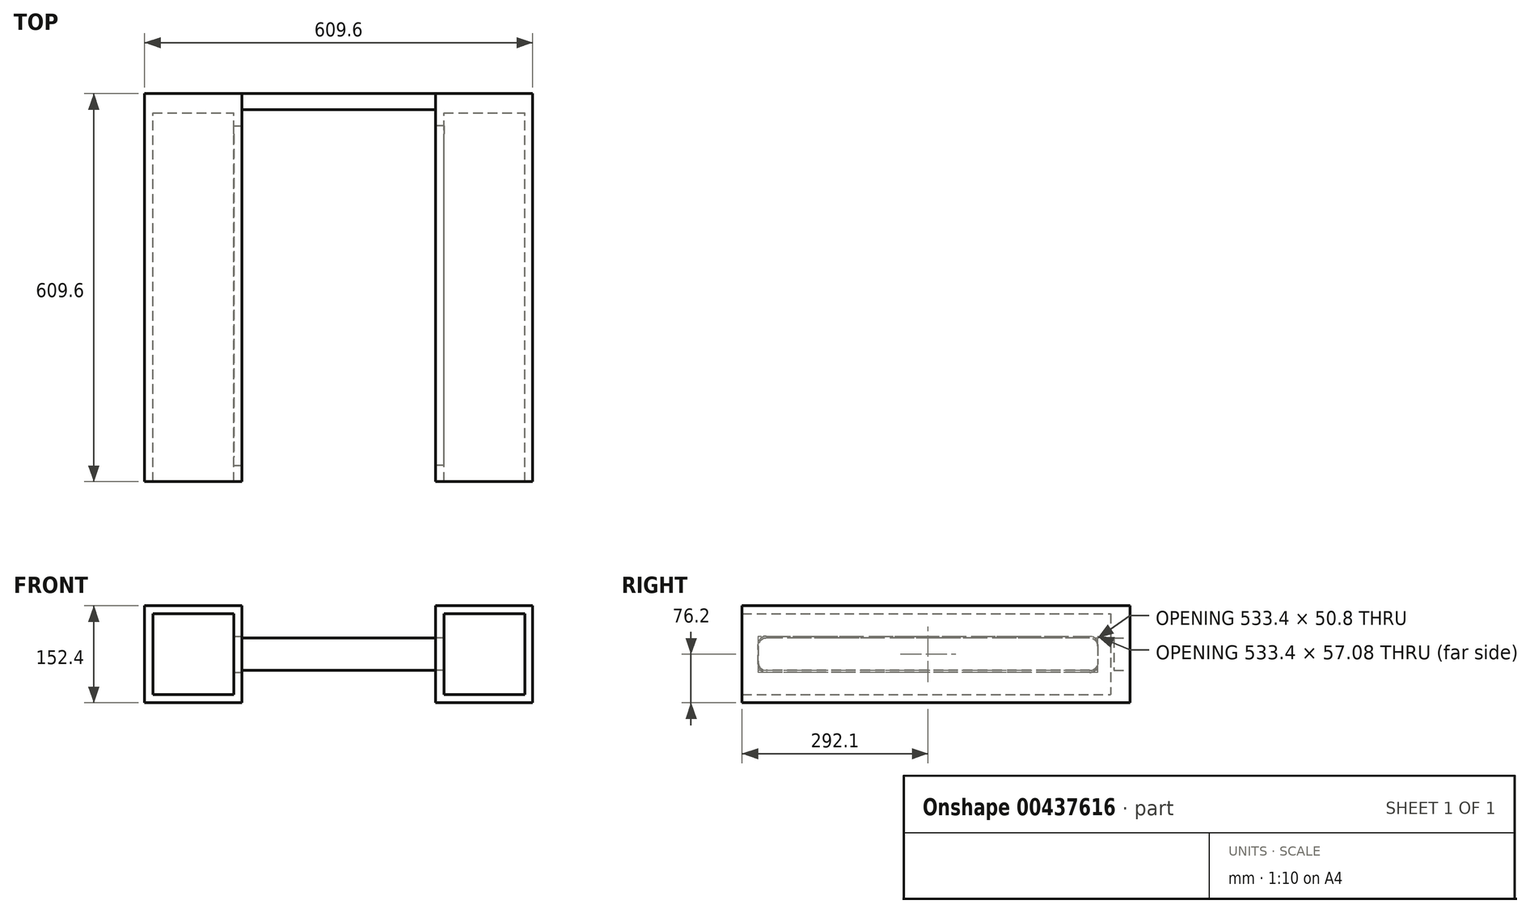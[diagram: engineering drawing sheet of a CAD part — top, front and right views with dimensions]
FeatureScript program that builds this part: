
annotation { "Feature Type Name" : "Feature", "Feature Type Description" : "" }
export const myFeature = defineFeature(function(context is Context, id is Id, definition is map)
    precondition{}
    {
        {
            var Q0;
            Q0=qCreatedBy(makeId("Front.planeOp"),FACE);
            var sketch = newSketch(context, id + "F0", { "sketchPlane" : qUnion([Q0])});
            skLineSegment(sketch, "E0.bottom", {"start": v(-398.61, -50.8) * mm, "end": v(-246.21, -50.8) * mm});
            skLineSegment(sketch, "E0.top", {"start": v(-398.61, 101.6) * mm, "end": v(-246.21, 101.6) * mm});
            skLineSegment(sketch, "E0.left", {"start": v(-398.61, -50.8) * mm, "end": v(-398.61, 101.6) * mm});
            skLineSegment(sketch, "E0.right", {"start": v(-246.21, -50.8) * mm, "end": v(-246.21, 101.6) * mm});
            skLineSegment(sketch, "E1.bottom", {"start": v(58.59, -50.8) * mm, "end": v(210.99, -50.8) * mm});
            skLineSegment(sketch, "E1.top", {"start": v(58.59, 101.6) * mm, "end": v(210.99, 101.6) * mm});
            skLineSegment(sketch, "E1.left", {"start": v(58.59, -50.8) * mm, "end": v(58.59, 101.6) * mm});
            skLineSegment(sketch, "E1.right", {"start": v(210.99, -50.8) * mm, "end": v(210.99, 101.6) * mm});
            skLineSegment(sketch, "E2.bottom", {"start": v(-385.91, -38.1) * mm, "end": v(-258.91, -38.1) * mm});
            skLineSegment(sketch, "E2.top", {"start": v(-385.91, 88.9) * mm, "end": v(-258.91, 88.9) * mm});
            skLineSegment(sketch, "E2.left", {"start": v(-385.91, -38.1) * mm, "end": v(-385.91, 88.9) * mm});
            skLineSegment(sketch, "E2.right", {"start": v(-258.91, -38.1) * mm, "end": v(-258.91, 88.9) * mm});
            skLineSegment(sketch, "E3.bottom", {"start": v(71.29, 88.9) * mm, "end": v(198.29, 88.9) * mm});
            skLineSegment(sketch, "E3.top", {"start": v(71.29, -38.1) * mm, "end": v(198.29, -38.1) * mm});
            skLineSegment(sketch, "E3.left", {"start": v(71.29, 88.9) * mm, "end": v(71.29, -38.1) * mm});
            skLineSegment(sketch, "E3.right", {"start": v(198.29, 88.9) * mm, "end": v(198.29, -38.1) * mm});
            skLineSegment(sketch, "E4", {"start": v(-246.21, 50.8) * mm, "end": v(58.59, 50.8) * mm});
            skLineSegment(sketch, "E5", {"start": v(-246.21, 0) * mm, "end": v(58.59, 0) * mm});
            skSolve(sketch);
        }
        {
            var Q0;
            {var subQ1=sQuery(id+"F0.wireOp",EDGE,"E0.bottom");Q0=makeQuery(id+"F0.imprint","IMPRINT",FACE,{"disambiguationData":[TD([[makeQuery(id+"F0.imprint","IMPRINT",EDGE,{"derivedFrom":subQ1}),1.0]])]});}
            var Q1;
            {var subQ0=sQuery(id+"F0.wireOp",EDGE,"E4");Q1=makeQuery(id+"F0.imprint","IMPRINT",FACE,{"disambiguationData":[TD([[makeQuery(id+"F0.imprint","IMPRINT",EDGE,{"derivedFrom":subQ0}),-1.0]])]});}
            var Q2;
            {var subQ3=sQuery(id+"F0.wireOp",EDGE,"E1.bottom");Q2=makeQuery(id+"F0.imprint","IMPRINT",FACE,{"disambiguationData":[TD([[makeQuery(id+"F0.imprint","IMPRINT",EDGE,{"derivedFrom":subQ3}),1.0]])]});}
            extrude(context, id + "F1", {"entities" : qUnion([Q0, Q1, Q2]), "depth" : 25.4 * mm});
        }
        {
            var Q0;
            Q0=makeQuery(id+"F0.imprint","IMPRINT",FACE,{"disambiguationData":[TD([[makeQuery(id+"F0.imprint","IMPRINT",EDGE,{"derivedFrom":sQuery(id+"F0.wireOp",EDGE,"E2.bottom")}),1.0]])]});
            var Q1;
            Q1=makeQuery(id+"F0.imprint","IMPRINT",FACE,{"disambiguationData":[TD([[makeQuery(id+"F0.imprint","IMPRINT",EDGE,{"derivedFrom":sQuery(id+"F0.wireOp",EDGE,"E3.bottom")}),-1.0]])]});
            extrude(context, id + "F2", {"entities" : qUnion([Q0, Q1]), "operationType" : NewBodyOperationType.ADD, "depth" : 30.48 * mm});
        }
        {
            var Q0;
            {var subQ1=sQuery(id+"F0.wireOp",EDGE,"E0.bottom");Q0=makeQuery(id+"F0.imprint","IMPRINT",FACE,{"disambiguationData":[TD([[makeQuery(id+"F0.imprint","IMPRINT",EDGE,{"derivedFrom":subQ1}),1.0]])]});}
            var Q1;
            {var subQ3=sQuery(id+"F0.wireOp",EDGE,"E1.bottom");Q1=makeQuery(id+"F0.imprint","IMPRINT",FACE,{"disambiguationData":[TD([[makeQuery(id+"F0.imprint","IMPRINT",EDGE,{"derivedFrom":subQ3}),1.0]])]});}
            extrude(context, id + "F3", {"entities" : qUnion([Q0, Q1]), "operationType" : NewBodyOperationType.ADD, "depth" : 609.6 * mm});
        }
        {
            var Q0;
            {var subQ0=sQuery(id+"F0.wireOp",EDGE,"E0.right");Q0=makeQuery(id+"F3.boolean.opBoolean","MERGE",FACE,{"derivedFrom":[makeQuery(id+"F1.opExtrude","SWEPT_FACE",FACE,{"disambiguationData":[OSD([subQ0]),TDD([makeQuery(id+"F0.imprint","IMPRINT",EDGE,{"disambiguationData":[TD([[makeQuery(id+"F0.imprint","INTERSECT",VERTEX,{"derivedFrom":[sQuery(id+"F0.wireOp",EDGE,"E0.bottom"),subQ0]}),-1.0]])],"derivedFrom":subQ0})])]}),makeQuery(id+"F1.opExtrude","SWEPT_FACE",FACE,{"disambiguationData":[OSD([subQ0]),TDD([makeQuery(id+"F0.imprint","IMPRINT",EDGE,{"disambiguationData":[TD([[makeQuery(id+"F0.imprint","INTERSECT",VERTEX,{"derivedFrom":[sQuery(id+"F0.wireOp",EDGE,"E0.top"),subQ0]}),1.0]])],"derivedFrom":subQ0})])]}),makeQuery(id+"F3.opExtrude","SWEPT_FACE",FACE,{"disambiguationData":[OSD([subQ0])]})]});}
            var sketch = newSketch(context, id + "F4", { "sketchPlane" : qUnion([Q0])});
            skLineSegment(sketch, "E6", {"start": v(-584.2, -3.14) * mm, "end": v(-584.2, 53.94) * mm});
            skLineSegment(sketch, "E7", {"start": v(-584.2, 53.94) * mm, "end": v(-50.8, 53.94) * mm});
            skLineSegment(sketch, "E8", {"start": v(-50.8, 53.94) * mm, "end": v(-50.8, -3.14) * mm});
            skLineSegment(sketch, "E9", {"start": v(-50.8, -3.14) * mm, "end": v(-584.2, -3.14) * mm});
            skSolve(sketch);
        }
        {
            var Q0;
            Q0=qSketchRegion(id+"F4",true);
            extrude(context, id + "F5", {"entities" : qUnion([Q0]), "operationType" : NewBodyOperationType.REMOVE, "oppositeDirection" : true, "depth" : 25.4 * mm});
        }
        {
            var Q0;
            Q0=makeQuery(id+"F5.boolean.opBoolean","COPY",EDGE,{"derivedFrom":makeQuery(id+"F5.opExtrude","SWEPT_EDGE",EDGE,{"disambiguationData":[OSD([sQuery(id+"F4.wireOp",EDGE,"E6"),sQuery(id+"F4.wireOp",EDGE,"E9")])]})});
            var Q1;
            Q1=makeQuery(id+"F5.boolean.opBoolean","COPY",EDGE,{"derivedFrom":makeQuery(id+"F5.opExtrude","SWEPT_EDGE",EDGE,{"disambiguationData":[OSD([sQuery(id+"F4.wireOp",EDGE,"E6"),sQuery(id+"F4.wireOp",EDGE,"E7")])]})});
            var Q2;
            Q2=makeQuery(id+"F5.boolean.opBoolean","COPY",EDGE,{"derivedFrom":makeQuery(id+"F5.opExtrude","SWEPT_EDGE",EDGE,{"disambiguationData":[OSD([sQuery(id+"F4.wireOp",EDGE,"E7"),sQuery(id+"F4.wireOp",EDGE,"E8")])]})});
            var Q3;
            Q3=makeQuery(id+"F5.boolean.opBoolean","COPY",EDGE,{"derivedFrom":makeQuery(id+"F5.opExtrude","SWEPT_EDGE",EDGE,{"disambiguationData":[OSD([sQuery(id+"F4.wireOp",EDGE,"E8"),sQuery(id+"F4.wireOp",EDGE,"E9")])]})});
            fillet(context, id + "F6", {"entities" : qUnion([Q0, Q1, Q2, Q3]), "radius" : 12.7 * mm, "tangentPropagation" : true, "allowEdgeOverflow" : false});
        }
        {
            var Q0;
            {var subQ0=sQuery(id+"F0.wireOp",EDGE,"E1.left");Q0=makeQuery(id+"F3.boolean.opBoolean","MERGE",FACE,{"derivedFrom":[makeQuery(id+"F1.opExtrude","SWEPT_FACE",FACE,{"disambiguationData":[OSD([subQ0]),TDD([makeQuery(id+"F0.imprint","IMPRINT",EDGE,{"disambiguationData":[TD([[makeQuery(id+"F0.imprint","INTERSECT",VERTEX,{"derivedFrom":[sQuery(id+"F0.wireOp",EDGE,"E1.bottom"),subQ0]}),-1.0]])],"derivedFrom":subQ0})])]}),makeQuery(id+"F1.opExtrude","SWEPT_FACE",FACE,{"disambiguationData":[OSD([subQ0]),TDD([makeQuery(id+"F0.imprint","IMPRINT",EDGE,{"disambiguationData":[TD([[makeQuery(id+"F0.imprint","INTERSECT",VERTEX,{"derivedFrom":[sQuery(id+"F0.wireOp",EDGE,"E1.top"),subQ0]}),1.0]])],"derivedFrom":subQ0})])]}),makeQuery(id+"F3.opExtrude","SWEPT_FACE",FACE,{"disambiguationData":[OSD([subQ0])]})]});}
            var sketch = newSketch(context, id + "F7", { "sketchPlane" : qUnion([Q0])});
            skLineSegment(sketch, "E10.bottom", {"start": v(50.8, 50.8) * mm, "end": v(584.2, 50.8) * mm});
            skLineSegment(sketch, "E10.top", {"start": v(50.8, 0) * mm, "end": v(584.2, 0) * mm});
            skLineSegment(sketch, "E10.left", {"start": v(50.8, 50.8) * mm, "end": v(50.8, 0) * mm});
            skLineSegment(sketch, "E10.right", {"start": v(584.2, 50.8) * mm, "end": v(584.2, 0) * mm});
            skSolve(sketch);
        }
        {
            var Q0;
            Q0=qSketchRegion(id+"F7",true);
            extrude(context, id + "F8", {"entities" : qUnion([Q0]), "operationType" : NewBodyOperationType.REMOVE, "oppositeDirection" : true, "depth" : 25.4 * mm});
        }
        {
            var Q0;
            Q0=makeQuery(id+"F8.boolean.opBoolean","COPY",EDGE,{"derivedFrom":makeQuery(id+"F8.opExtrude","SWEPT_EDGE",EDGE,{"disambiguationData":[OSD([sQuery(id+"F7.wireOp",EDGE,"E10.bottom"),sQuery(id+"F7.wireOp",EDGE,"E10.right")])]})});
            var Q1;
            Q1=makeQuery(id+"F8.boolean.opBoolean","COPY",EDGE,{"derivedFrom":makeQuery(id+"F8.opExtrude","SWEPT_EDGE",EDGE,{"disambiguationData":[OSD([sQuery(id+"F7.wireOp",EDGE,"E10.top"),sQuery(id+"F7.wireOp",EDGE,"E10.right")])]})});
            var Q2;
            Q2=makeQuery(id+"F8.boolean.opBoolean","COPY",EDGE,{"derivedFrom":makeQuery(id+"F8.opExtrude","SWEPT_EDGE",EDGE,{"disambiguationData":[OSD([sQuery(id+"F7.wireOp",EDGE,"E10.top"),sQuery(id+"F7.wireOp",EDGE,"E10.left")])]})});
            var Q3;
            Q3=makeQuery(id+"F8.boolean.opBoolean","COPY",EDGE,{"derivedFrom":makeQuery(id+"F8.opExtrude","SWEPT_EDGE",EDGE,{"disambiguationData":[OSD([sQuery(id+"F7.wireOp",EDGE,"E10.bottom"),sQuery(id+"F7.wireOp",EDGE,"E10.left")])]})});
            fillet(context, id + "F9", {"entities" : qUnion([Q0, Q1, Q2, Q3]), "radius" : 12.7 * mm, "tangentPropagation" : true, "allowEdgeOverflow" : false});
        }
    });
